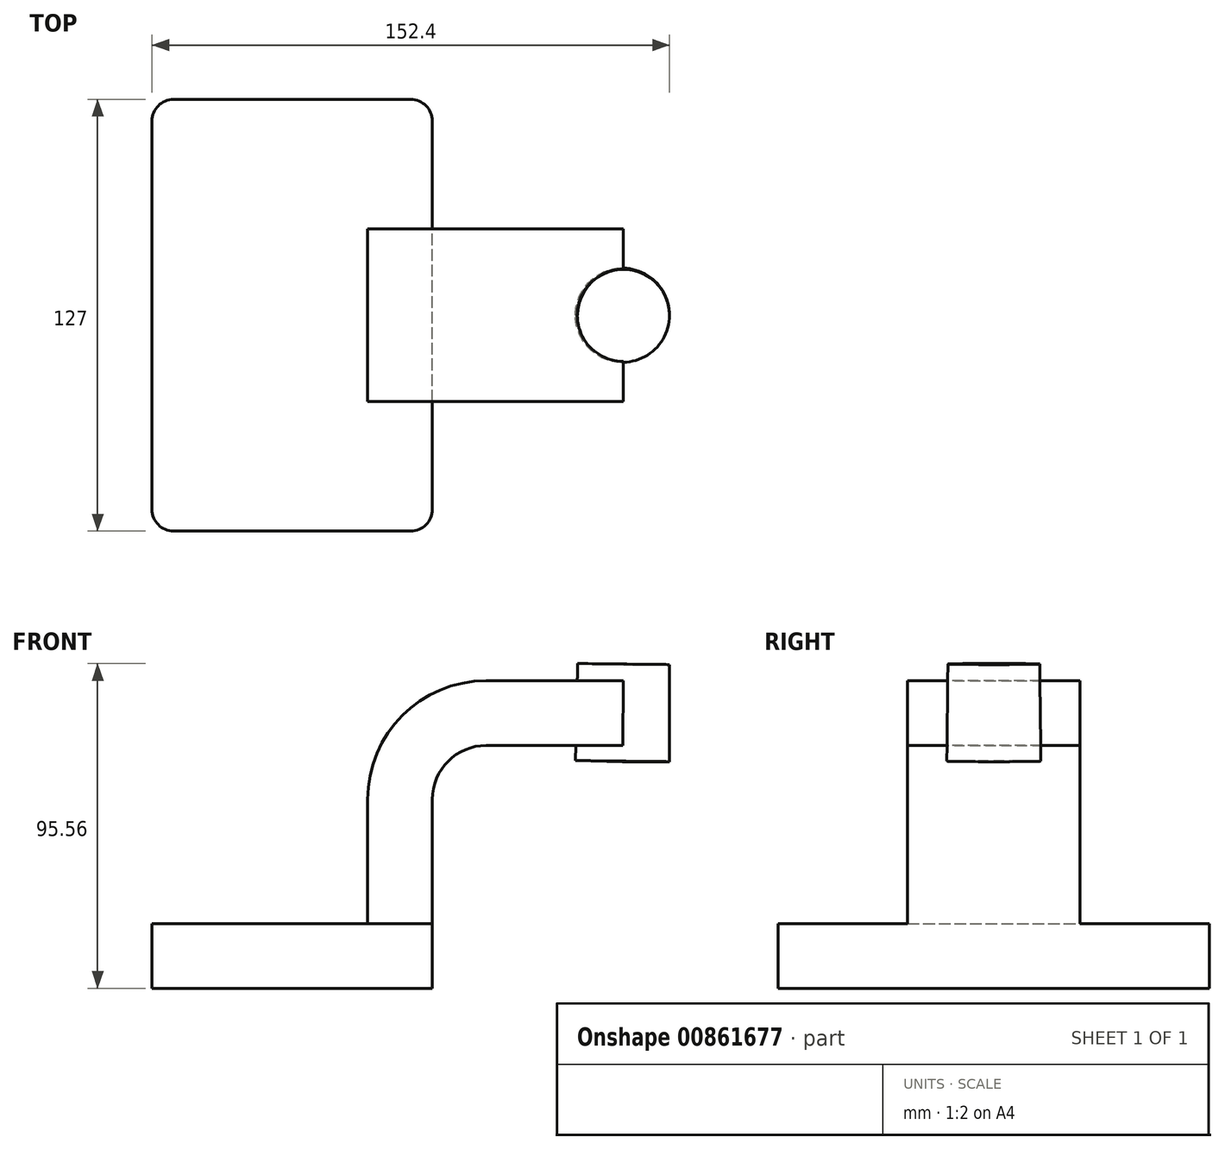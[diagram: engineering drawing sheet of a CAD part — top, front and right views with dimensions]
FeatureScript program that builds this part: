
annotation { "Feature Type Name" : "Feature", "Feature Type Description" : "" }
export const myFeature = defineFeature(function(context is Context, id is Id, definition is map)
    precondition{}
    {
        {
            var Q0;
            Q0=qCreatedBy(makeId("Front.planeOp"),FACE);
            var sketch = newSketch(context, id + "F0", { "sketchPlane" : qUnion([Q0])});
            skLineSegment(sketch, "E0.bottom", {"start": v(41.28, -9.52) * mm, "end": v(-41.28, -9.53) * mm});
            skLineSegment(sketch, "E0.top", {"start": v(41.28, 9.53) * mm, "end": v(-41.28, 9.53) * mm});
            skLineSegment(sketch, "E0.left", {"start": v(41.28, -9.52) * mm, "end": v(41.28, 9.53) * mm});
            skLineSegment(sketch, "E0.right", {"start": v(-41.28, -9.52) * mm, "end": v(-41.28, 9.53) * mm});
            skPoint(sketch, "E0.middle", {"position": v(0, 0) * mm});
            skLineSegment(sketch, "E1.bottom", {"start": v(60.32, 57.15) * mm, "end": v(111.12, 57.15) * mm});
            skLineSegment(sketch, "E1.top", {"start": v(60.32, 85.73) * mm, "end": v(111.12, 85.73) * mm});
            skLineSegment(sketch, "E1.left", {"start": v(60.32, 57.15) * mm, "end": v(60.32, 85.73) * mm});
            skLineSegment(sketch, "E1.right", {"start": v(111.12, 57.15) * mm, "end": v(111.12, 85.73) * mm});
            skPoint(sketch, "E1.middle", {"position": v(85.72, 71.44) * mm});
            skLineSegment(sketch, "E2", {"start": v(41.28, 9.53) * mm, "end": v(41.28, 46.05) * mm});
            skArc(sketch, "E3", {"start": v(41.27, 46.05) * mm, "mid": v(45.92, 57.28) * mm, "end": v(57.15, 61.93) * mm});
            skLineSegment(sketch, "E4", {"start": v(57.15, 61.93) * mm, "end": v(97.6, 61.93) * mm});
            skLineSegment(sketch, "E5.0", {"start": v(57.15, 80.98) * mm, "end": v(97.6, 80.98) * mm});
            skArc(sketch, "E5.1", {"start": v(22.23, 46.05) * mm, "mid": v(32.45, 70.75) * mm, "end": v(57.15, 80.98) * mm});
            skLineSegment(sketch, "E5.2", {"start": v(22.22, 9.53) * mm, "end": v(22.22, 46.05) * mm});
            skLineSegment(sketch, "E6", {"start": v(97.27, 57.15) * mm, "end": v(97.6, 85.73) * mm});
            skFitSpline(sketch, "E7", {"points": [v(-41.28, 9.52) * mm, v(57.15, 80.98) * mm], "startDerivative": vector(33.03, 108.86) * mm, "endDerivative": vector(206.48, -1.62) * mm});
            skSolve(sketch);
        }
        {
            var Q0;
            Q0=makeQuery(id+"F0.imprint","IMPRINT",FACE,{"disambiguationData":[TD([[makeQuery(id+"F0.imprint","IMPRINT",EDGE,{"derivedFrom":sQuery(id+"F0.wireOp",EDGE,"E0.bottom")}),-1.0]])]});
            extrude(context, id + "F1", {"entities" : qUnion([Q0]), "endBound" : BoundingType.SYMMETRIC, "depth" : 127 * mm, "offsetDistance" : 25.4 * mm});
        }
        {
            var Q0;
            {var subQ1=sQuery(id+"F0.wireOp",EDGE,"E2");Q0=makeQuery(id+"F0.imprint","IMPRINT",FACE,{"disambiguationData":[TD([[makeQuery(id+"F0.imprint","IMPRINT",EDGE,{"derivedFrom":subQ1}),1.0]])]});}
            var Q1;
            {var subQ0=sQuery(id+"F0.wireOp",EDGE,"E4");var subQ1=sQuery(id+"F0.wireOp",EDGE,"E1.left");var subQ2=makeQuery(id+"F0.imprint","INTERSECT",VERTEX,{"derivedFrom":[subQ1,subQ0]});Q1=makeQuery(id+"F0.imprint","IMPRINT",FACE,{"disambiguationData":[TD([[makeQuery(id+"F0.imprint","IMPRINT",EDGE,{"disambiguationData":[TD([[subQ2,-1.0]])],"derivedFrom":subQ1}),-1.0]])]});}
            extrude(context, id + "F2", {"entities" : qUnion([Q0, Q1]), "operationType" : NewBodyOperationType.ADD, "endBound" : BoundingType.SYMMETRIC, "depth" : 50.8 * mm, "offsetDistance" : 25.4 * mm});
        }
        {
            var Q0;
            Q0=makeQuery(id+"F0.imprint","IMPRINT",FACE,{"disambiguationData":[TD([[makeQuery(id+"F0.imprint","IMPRINT",EDGE,{"derivedFrom":sQuery(id+"F0.wireOp",EDGE,"E5.1")}),1.0]])]});
            extrude(context, id + "F3", {"entities" : qUnion([Q0]), "operationType" : NewBodyOperationType.ADD, "endBound" : BoundingType.SYMMETRIC, "depth" : 15.88 * mm, "offsetDistance" : 25.4 * mm});
        }
        {
            var Q0;
            {var subQ0=sQuery(id+"F0.wireOp",EDGE,"E1.right");Q0=makeQuery(id+"F0.imprint","IMPRINT",FACE,{"disambiguationData":[TD([[makeQuery(id+"F0.imprint","IMPRINT",EDGE,{"derivedFrom":subQ0}),1.0]])]});}
            var Q1;
            Q1=sQuery(id+"F0.wireOp",EDGE,"E6");
            revolve(context, id + "F4", {"operationType" : NewBodyOperationType.ADD, "surfaceOperationType" : NewSurfaceOperationType.NEW, "entities" : qUnion([Q0]), "axis" : qUnion([Q1]), "revolveType" : RevolveType.FULL});
        }
        {
            var Q0;
            Q0=makeQuery(id+"F1.opExtrude","CAP_EDGE",EDGE,{"disambiguationData":[OSD([sQuery(id+"F0.wireOp",EDGE,"E0.left")])],"isStart":false});
            var Q1;
            Q1=makeQuery(id+"F1.opExtrude","CAP_EDGE",EDGE,{"disambiguationData":[OSD([sQuery(id+"F0.wireOp",EDGE,"E0.right")])],"isStart":false});
            var Q2;
            Q2=makeQuery(id+"F1.opExtrude","CAP_EDGE",EDGE,{"disambiguationData":[OSD([sQuery(id+"F0.wireOp",EDGE,"E0.left")])],"isStart":true});
            var Q3;
            Q3=makeQuery(id+"F1.opExtrude","CAP_EDGE",EDGE,{"disambiguationData":[OSD([sQuery(id+"F0.wireOp",EDGE,"E0.right")])],"isStart":true});
            fillet(context, id + "F5", {"entities" : qUnion([Q0, Q1, Q2, Q3]), "radius" : 6.35 * mm, "tangentPropagation" : true, "allowEdgeOverflow" : false});
        }
    });
